# Revit family: CONV_Pholc_GnrlPrpseLmnrs_Kadinsky30
name_source: partatom
category: Lighting Fixtures
revit_build: Autodesk Revit 2017 (Build: 20160225_1515(x64)
units: mm (PartAtom-declared; Revit-internal decimal feet)

## family parameters
Always vertical = Yes
Cut with Voids When Loaded = No
Host = Ceiling
Light Source = Yes
OmniClass Number = 23.80.70.11
OmniClass Title = Luminaries for Internal Lighting
Part Type = Normal
Room Calculation Point = No
Round Connector Dimension = Use Diameter
Shared = No

## types (2) — shared parameters
AssetType = Fixed
BIMObjectName = CONV_Pholc_GnrlPrpseLmnrs_Kadinsky30
Brand = Pholc
Category = Pendant
Collection = Kandinsky
Color = Various
Color Filter = 16777215
ConvergoRefNr = 0103-1905-0001-SE
Description = This pendant lamp is inspired by the abstract circle paintings by Wassily Kandinsky during his years at the renowned Bauhaus school  in the 1920´s. A sphere and a spear act as the main characters in the lamps composition, piercing each other in mid air to create an object that evokes a sensation of weightlessness, fragility and precision.
The custom made light source is shaped and fitted seamlessly as a part of the brass spear and emits a glowing dimmable light from within the centre in the smoke colored glass.
The Kandinsky lamp comes in two sizes with a 300 or 450mm wide glass bubble. It functions well as a lamp or object to set the mood of a room, hanging in numbers in a big space or as a single piece over a table.
Designer = Broberg & Ridderstrale
Dimming Lamp Color Temperature Shift = <None>
DurationUnit = Year
Features = Suspension mounting. Textile cable: black. Ceiling cup: black
HasProtectiveEarth = No
IP_Code = IP 20
IfcExportAs = IfcLightFixtureType
IfcExportType = NOTDEFINED
InsulationStandardClass = Class II
Light Source Symbol Size = 610 mm
LightFixtureMainMaterial = Brass
LightFixtureMountingType = Suspended
LightFixturePlacingType = Ceiling
LightFixtureSecondaryMaterial = Black
LightSource = Exchangeble lightsource – LED, W: 5 LM: 417 K:2700 CRI: 80 dimmable
Manufacturer = Pholc
ManufacturerName = Pholc
ManufacturerURL = https://www.pholc.se
Material = Brass, glass & textile
NBSDescription = General purpose luminaires
NBSReference = 90-60-50/405
Name = GnrlPrpseLmnrs_Kadinsky30
NominalCurrent = 0 A
NominalDepth = 300 mm
NominalDiameter = 300 mm
NominalFrequencyRange = 0 Hz
NominalRadius = 150 mm
NominalVoltage = 0 V
NominalVoltageCalc = 0 V
NominalWidth = 300 mm
NumberOfPoles = 1
PhaseAngle = 0.00°
ProductDatasheet = https://www.pholc.se
ProductInformation = It functions well as a lamp or object to set the mood of a room, hanging in numbers in a large space or as a single piece over a table.
Shape = Sculptured
Size = 300x300x800 mm
TotalWattage = 5 W
URL = https://www.pholc.se
Uniclass2 = Pr_70_70_49_86
Uniclass2015Description = Suspended luminaires
Uniclass2015Reference = Pr_70_70_48_86
UsageCurrent = 0 A
Version = 1
VersionDate = 14/05/2019
WarrantyDurationUnit = Year
zero-valued in all types: DefaultElevation, ElectricalDeviceNominalPower, MaintenanceFactor, NumberOfSources

## per-type parameters (varying)
| type | ArticleNumber | LensMaterial | ModelReference |
| Kandinsky 30 smoked grey | 517119 | Glass smoked grey | 517119 |
| Kandinsky 30 smoked brown | 517112 | Glass smoked brown | 517112 |

note: column(s) folded — value = type name in every type: Model

## geometry (parser evidence)
native form markers: Sweep x5
no freeform markers — native parametric forms only
